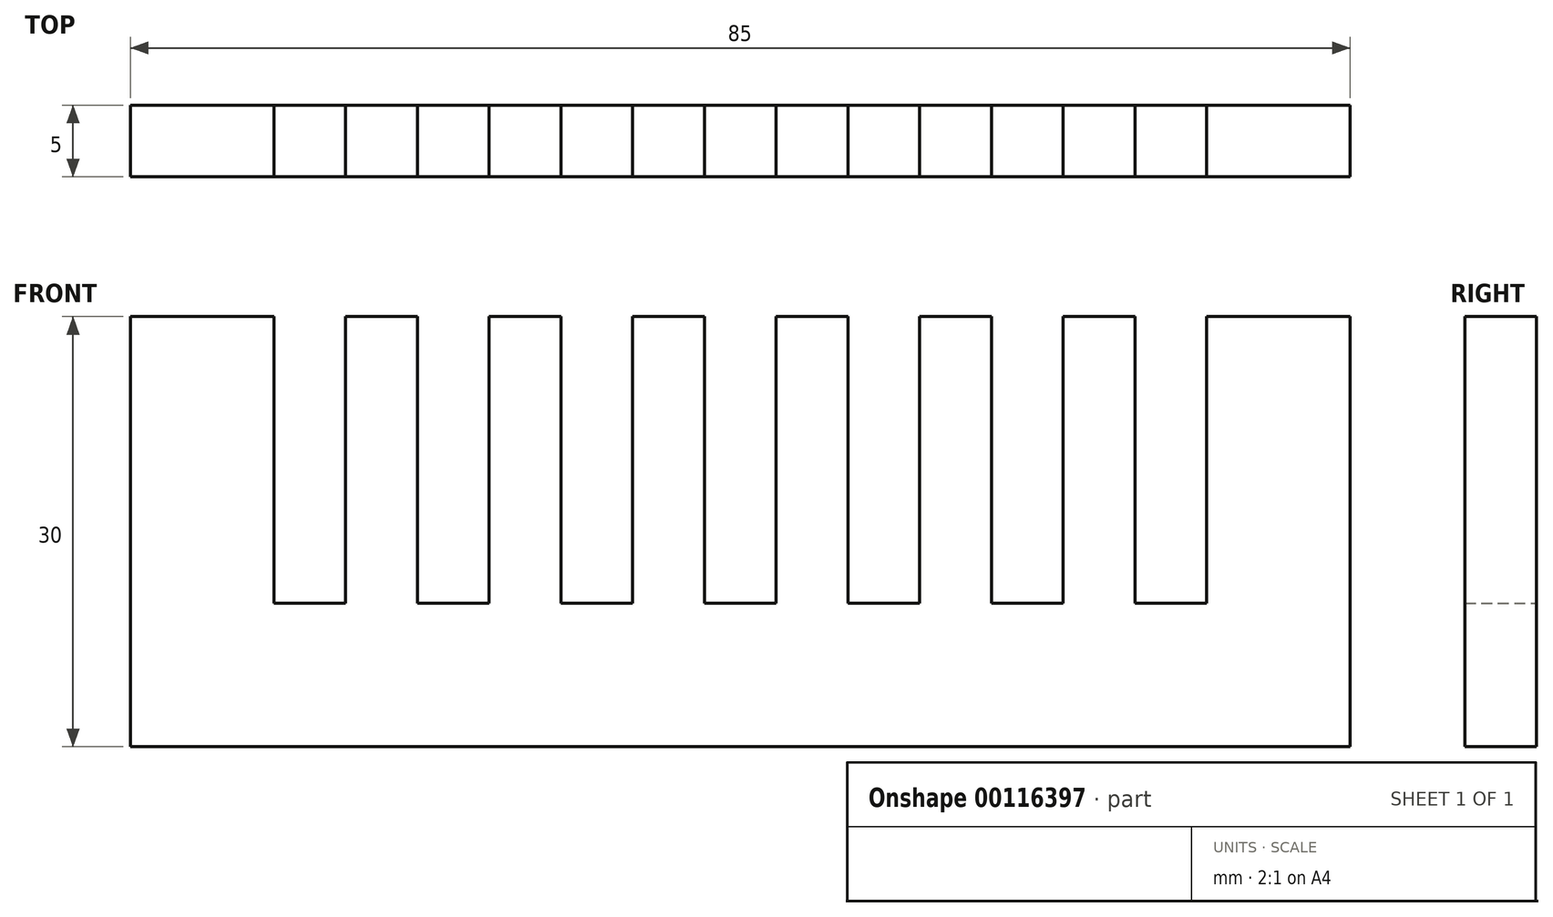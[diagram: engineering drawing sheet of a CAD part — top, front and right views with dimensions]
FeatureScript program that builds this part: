
annotation { "Feature Type Name" : "Feature", "Feature Type Description" : "" }
export const myFeature = defineFeature(function(context is Context, id is Id, definition is map)
    precondition{}
    {
        {
            var Q0;
            Q0=qCreatedBy(makeId("Front.planeOp"),FACE);
            var sketch = newSketch(context, id + "F0", { "sketchPlane" : qUnion([Q0])});
            skLineSegment(sketch, "E0.bottom", {"start": v(42.5, -5) * mm, "end": v(-42.5, -5) * mm});
            skLineSegment(sketch, "E0.top", {"start": v(42.5, 5) * mm, "end": v(-42.5, 5) * mm});
            skLineSegment(sketch, "E0.left", {"start": v(42.5, -5) * mm, "end": v(42.5, 5) * mm});
            skLineSegment(sketch, "E0.right", {"start": v(-42.5, -5) * mm, "end": v(-42.5, 5) * mm});
            skPoint(sketch, "E0.middle", {"position": v(0, 0) * mm});
            skLineSegment(sketch, "E1.bottom", {"start": v(-42.5, 5) * mm, "end": v(-32.5, 5) * mm});
            skLineSegment(sketch, "E1.top", {"start": v(-42.5, 25) * mm, "end": v(-32.5, 25) * mm});
            skLineSegment(sketch, "E1.left", {"start": v(-42.5, 5) * mm, "end": v(-42.5, 25) * mm});
            skLineSegment(sketch, "E1.right", {"start": v(-32.5, 5) * mm, "end": v(-32.5, 25) * mm});
            skLineSegment(sketch, "E2.bottom", {"start": v(42.5, 5) * mm, "end": v(32.5, 5) * mm});
            skLineSegment(sketch, "E2.top", {"start": v(42.5, 25) * mm, "end": v(32.5, 25) * mm});
            skLineSegment(sketch, "E2.left", {"start": v(42.5, 5) * mm, "end": v(42.5, 25) * mm});
            skLineSegment(sketch, "E2.right", {"start": v(32.5, 5) * mm, "end": v(32.5, 25) * mm});
            skLineSegment(sketch, "E3.bottom", {"start": v(-32.5, 5) * mm, "end": v(-27.5, 5) * mm});
            skLineSegment(sketch, "E3.right", {"start": v(-27.5, 5) * mm, "end": v(-27.5, 25) * mm});
            skLineSegment(sketch, "E4.bottom", {"start": v(-27.5, 5) * mm, "end": v(-22.5, 5) * mm});
            skLineSegment(sketch, "E4.top", {"start": v(-27.5, 25) * mm, "end": v(-22.5, 25) * mm});
            skLineSegment(sketch, "E4.right", {"start": v(-22.5, 5) * mm, "end": v(-22.5, 25) * mm});
            skLineSegment(sketch, "E5.bottom", {"start": v(-22.5, 5) * mm, "end": v(-17.5, 5) * mm});
            skLineSegment(sketch, "E5.right", {"start": v(-17.5, 5) * mm, "end": v(-17.5, 25) * mm});
            skLineSegment(sketch, "E6.bottom", {"start": v(-17.5, 5) * mm, "end": v(-12.5, 5) * mm});
            skLineSegment(sketch, "E6.right", {"start": v(-12.5, 5) * mm, "end": v(-12.5, 25) * mm});
            skLineSegment(sketch, "E7.bottom", {"start": v(-12.5, 5) * mm, "end": v(-7.5, 5) * mm});
            skLineSegment(sketch, "E7.right", {"start": v(-7.5, 5) * mm, "end": v(-7.5, 25) * mm});
            skLineSegment(sketch, "E8.bottom", {"start": v(-7.5, 5) * mm, "end": v(-2.5, 5) * mm});
            skLineSegment(sketch, "E8.top", {"start": v(-7.5, 25) * mm, "end": v(-2.5, 25) * mm});
            skLineSegment(sketch, "E8.right", {"start": v(-2.5, 5) * mm, "end": v(-2.5, 25) * mm});
            skLineSegment(sketch, "E9.bottom", {"start": v(-2.5, 5) * mm, "end": v(2.5, 5) * mm});
            skLineSegment(sketch, "E9.right", {"start": v(2.5, 5) * mm, "end": v(2.5, 25) * mm});
            skLineSegment(sketch, "E10.bottom", {"start": v(2.5, 5) * mm, "end": v(7.5, 5) * mm});
            skLineSegment(sketch, "E10.top", {"start": v(2.5, 25) * mm, "end": v(7.5, 25) * mm});
            skLineSegment(sketch, "E10.right", {"start": v(7.5, 5) * mm, "end": v(7.5, 25) * mm});
            skLineSegment(sketch, "E11.bottom", {"start": v(7.5, 5) * mm, "end": v(12.5, 5) * mm});
            skLineSegment(sketch, "E11.right", {"start": v(12.5, 5) * mm, "end": v(12.5, 25) * mm});
            skLineSegment(sketch, "E12.bottom", {"start": v(12.5, 5) * mm, "end": v(17.5, 5) * mm});
            skLineSegment(sketch, "E12.top", {"start": v(12.5, 25) * mm, "end": v(17.5, 25) * mm});
            skLineSegment(sketch, "E12.right", {"start": v(17.5, 5) * mm, "end": v(17.5, 25) * mm});
            skLineSegment(sketch, "E13.bottom", {"start": v(17.5, 5) * mm, "end": v(22.5, 5) * mm});
            skLineSegment(sketch, "E13.right", {"start": v(22.5, 5) * mm, "end": v(22.5, 25) * mm});
            skLineSegment(sketch, "E14.bottom", {"start": v(22.5, 5) * mm, "end": v(27.5, 5) * mm});
            skLineSegment(sketch, "E14.top", {"start": v(22.5, 25) * mm, "end": v(27.5, 25) * mm});
            skLineSegment(sketch, "E14.right", {"start": v(27.5, 5) * mm, "end": v(27.5, 25) * mm});
            skLineSegment(sketch, "E15", {"start": v(-17.5, 25) * mm, "end": v(-12.5, 25) * mm});
            skSolve(sketch);
        }
        {
            var Q0;
            Q0 = qSketchRegion(id + "F0", true);
            extrude(context, id + "F1", {"entities" : qUnion([Q0]), "endBound" : BoundingType.SYMMETRIC, "depth" : 5 * mm});
        }
    });
